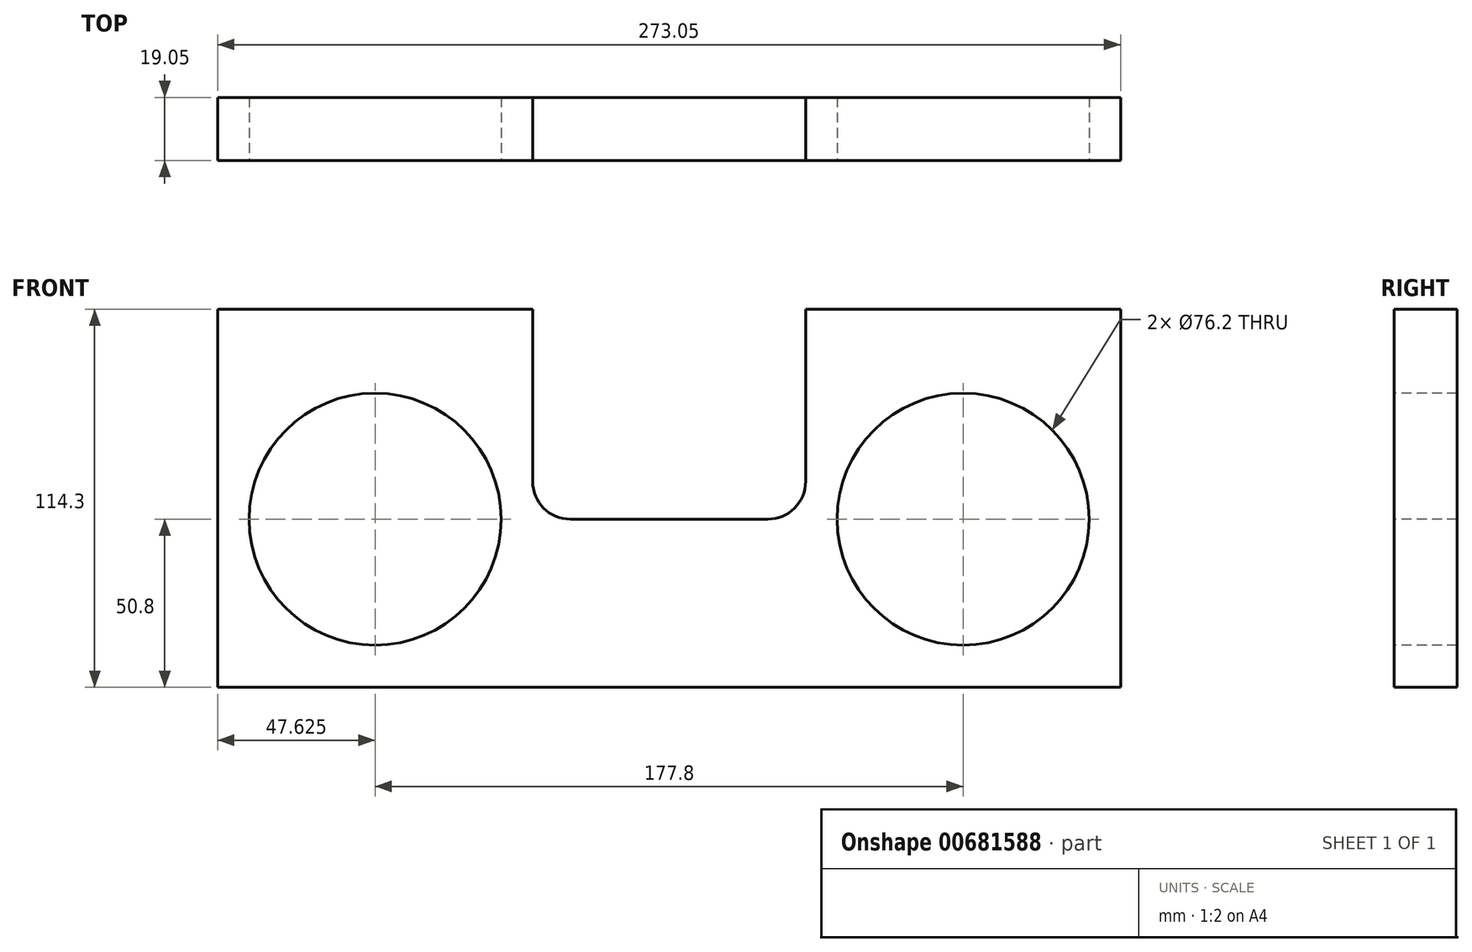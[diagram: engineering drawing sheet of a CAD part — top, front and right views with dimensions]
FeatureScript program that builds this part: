
annotation { "Feature Type Name" : "Feature", "Feature Type Description" : "" }
export const myFeature = defineFeature(function(context is Context, id is Id, definition is map)
    precondition{}
    {
        {
            var Q0;
            Q0=qCreatedBy(makeId("Front.planeOp"),FACE);
            var sketch = newSketch(context, id + "F0", { "sketchPlane" : qUnion([Q0])});
            skLineSegment(sketch, "E0.bottom", {"start": v(0, 0) * mm, "end": v(273.05, 0) * mm});
            skLineSegment(sketch, "E0.top", {"start": v(0, 114.3) * mm, "end": v(273.05, 114.3) * mm});
            skLineSegment(sketch, "E0.left", {"start": v(0, 0) * mm, "end": v(0, 114.3) * mm});
            skLineSegment(sketch, "E0.right", {"start": v(273.05, 0) * mm, "end": v(273.05, 114.3) * mm});
            skSolve(sketch);
        }
        {
            var Q0;
            Q0=qSketchRegion(id+"F0",true);
            extrude(context, id + "F1", {"entities" : qUnion([Q0]), "depth" : 19.05 * mm, "offsetDistance" : 25.4 * mm});
        }
        {
            var Q0;
            Q0=makeQuery(id+"F1.opExtrude","CAP_FACE",FACE,{"disambiguationData":[OSD([sQuery(id+"F0.wireOp",EDGE,"E0.bottom"),sQuery(id+"F0.wireOp",EDGE,"E0.top"),sQuery(id+"F0.wireOp",EDGE,"E0.left"),sQuery(id+"F0.wireOp",EDGE,"E0.right")])],"isStart":false});
            var sketch = newSketch(context, id + "F2", { "sketchPlane" : qUnion([Q0])});
            skCircle(sketch, "E1", {"center": v(47.63, 50.8) * mm, "radius": 38.1 * mm});
            skCircle(sketch, "E2", {"center": v(225.43, 50.8) * mm, "radius": 38.1 * mm});
            skSolve(sketch);
        }
        {
            var Q0;
            Q0=makeQuery(id+"F2.imprint","IMPRINT",FACE,{"disambiguationData":[TD([[makeQuery(id+"F2.imprint","IMPRINT",EDGE,{"derivedFrom":sQuery(id+"F2.wireOp",EDGE,"E2")}),1.0]])]});
            var Q1;
            Q1=makeQuery(id+"F2.imprint","IMPRINT",FACE,{"disambiguationData":[TD([[makeQuery(id+"F2.imprint","IMPRINT",EDGE,{"derivedFrom":sQuery(id+"F2.wireOp",EDGE,"E1")}),1.0]])]});
            extrude(context, id + "F3", {"entities" : qUnion([Q0, Q1]), "operationType" : NewBodyOperationType.REMOVE, "oppositeDirection" : true, "depth" : 25.4 * mm, "offsetDistance" : 25.4 * mm});
        }
        {
            var Q0;
            Q0=makeQuery(id+"F1.opExtrude","CAP_FACE",FACE,{"disambiguationData":[OSD([sQuery(id+"F0.wireOp",EDGE,"E0.bottom"),sQuery(id+"F0.wireOp",EDGE,"E0.top"),sQuery(id+"F0.wireOp",EDGE,"E0.left"),sQuery(id+"F0.wireOp",EDGE,"E0.right")])],"isStart":false});
            var sketch = newSketch(context, id + "F4", { "sketchPlane" : qUnion([Q0])});
            skLineSegment(sketch, "E3", {"start": v(95.25, 114.3) * mm, "end": v(95.25, 62.23) * mm});
            skLineSegment(sketch, "E4", {"start": v(106.68, 50.8) * mm, "end": v(166.37, 50.8) * mm});
            skLineSegment(sketch, "E5", {"start": v(177.8, 62.23) * mm, "end": v(177.8, 114.3) * mm});
            skPoint(sketch, "E6.visualSharp", {"position": v(95.25, 50.8) * mm});
            skArc(sketch, "E6.filletArc", {"start": v(95.25, 62.23) * mm, "mid": v(98.6, 54.15) * mm, "end": v(106.68, 50.8) * mm});
            skPoint(sketch, "E7.visualSharp", {"position": v(177.8, 50.8) * mm});
            skArc(sketch, "E7.filletArc", {"start": v(166.37, 50.8) * mm, "mid": v(174.45, 54.15) * mm, "end": v(177.8, 62.23) * mm});
            skSolve(sketch);
        }
        {
            var Q0;
            {var subQ1=sQuery(id+"F4.wireOp",EDGE,"E3");Q0=makeQuery(id+"F4.imprint","IMPRINT",FACE,{"disambiguationData":[TD([[makeQuery(id+"F4.imprint","IMPRINT",EDGE,{"derivedFrom":subQ1}),1.0]])]});}
            extrude(context, id + "F5", {"entities" : qUnion([Q0]), "operationType" : NewBodyOperationType.REMOVE, "oppositeDirection" : true, "depth" : 25.4 * mm, "offsetDistance" : 25.4 * mm});
        }
    });
